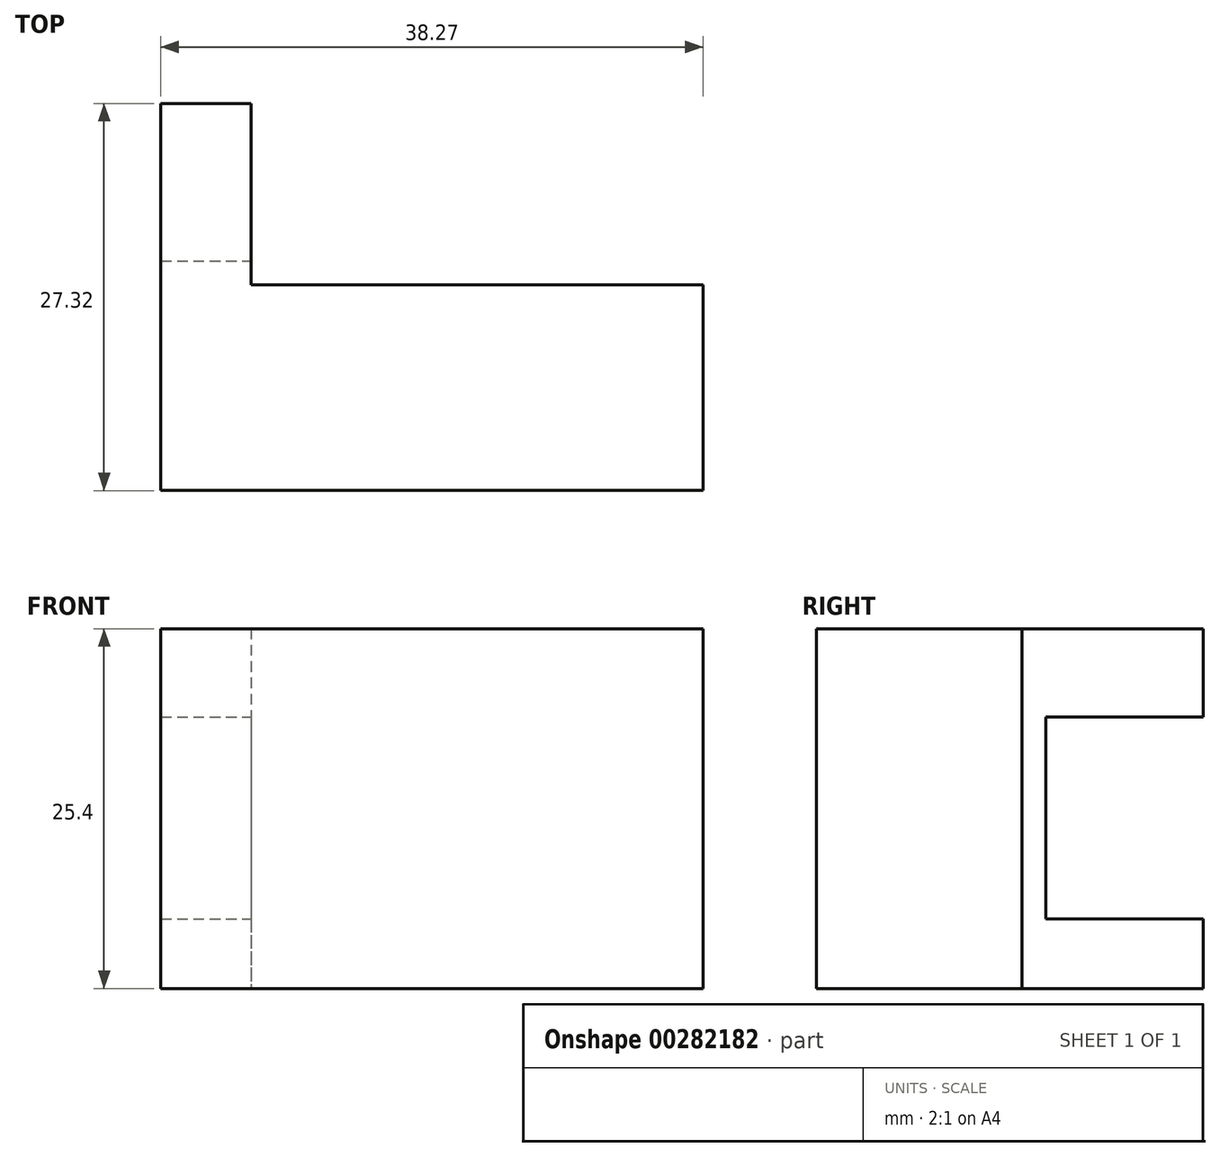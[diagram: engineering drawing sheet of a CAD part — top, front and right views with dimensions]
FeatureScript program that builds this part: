
annotation { "Feature Type Name" : "Feature", "Feature Type Description" : "" }
export const myFeature = defineFeature(function(context is Context, id is Id, definition is map)
    precondition{}
    {
        {
            var Q0;
            Q0=qCreatedBy(makeId("Top.planeOp"),FACE);
            var sketch = newSketch(context, id + "F0", { "sketchPlane" : qUnion([Q0])});
            skLineSegment(sketch, "E0", {"start": v(0, 0) * mm, "end": v(0, -27.32) * mm});
            skLineSegment(sketch, "E1", {"start": v(0, -27.32) * mm, "end": v(38.27, -27.32) * mm});
            skLineSegment(sketch, "E2", {"start": v(0, 0) * mm, "end": v(6.38, 0) * mm});
            skLineSegment(sketch, "E3", {"start": v(6.38, 0) * mm, "end": v(6.38, -12.8) * mm});
            skLineSegment(sketch, "E4", {"start": v(6.38, -12.8) * mm, "end": v(38.27, -12.8) * mm});
            skLineSegment(sketch, "E5", {"start": v(38.27, -12.8) * mm, "end": v(38.27, -27.32) * mm});
            skSolve(sketch);
        }
        {
            var Q0;
            Q0 = qSketchRegion(id + "F0", true);
            extrude(context, id + "F1", {"entities" : qUnion([Q0]), "depth" : 25.4 * mm});
        }
        {
            var Q0;
            Q0=qCreatedBy(makeId("Right.planeOp"),FACE);
            var sketch = newSketch(context, id + "F2", { "sketchPlane" : qUnion([Q0])});
            skLineSegment(sketch, "E6.bottom", {"start": v(0, 19.15) * mm, "end": v(-11.13, 19.15) * mm});
            skLineSegment(sketch, "E6.top", {"start": v(0, 4.91) * mm, "end": v(-11.13, 4.91) * mm});
            skLineSegment(sketch, "E6.left", {"start": v(0, 19.15) * mm, "end": v(0, 4.91) * mm});
            skLineSegment(sketch, "E6.right", {"start": v(-11.13, 19.15) * mm, "end": v(-11.13, 4.91) * mm});
            skSolve(sketch);
        }
        {
            var Q0;
            Q0 = qSketchRegion(id + "F2", true);
            extrude(context, id + "F3", {"entities" : qUnion([Q0]), "operationType" : NewBodyOperationType.REMOVE, "endBound" : BoundingType.SYMMETRIC, "oppositeDirection" : true, "depth" : 170.18 * mm});
        }
    });
